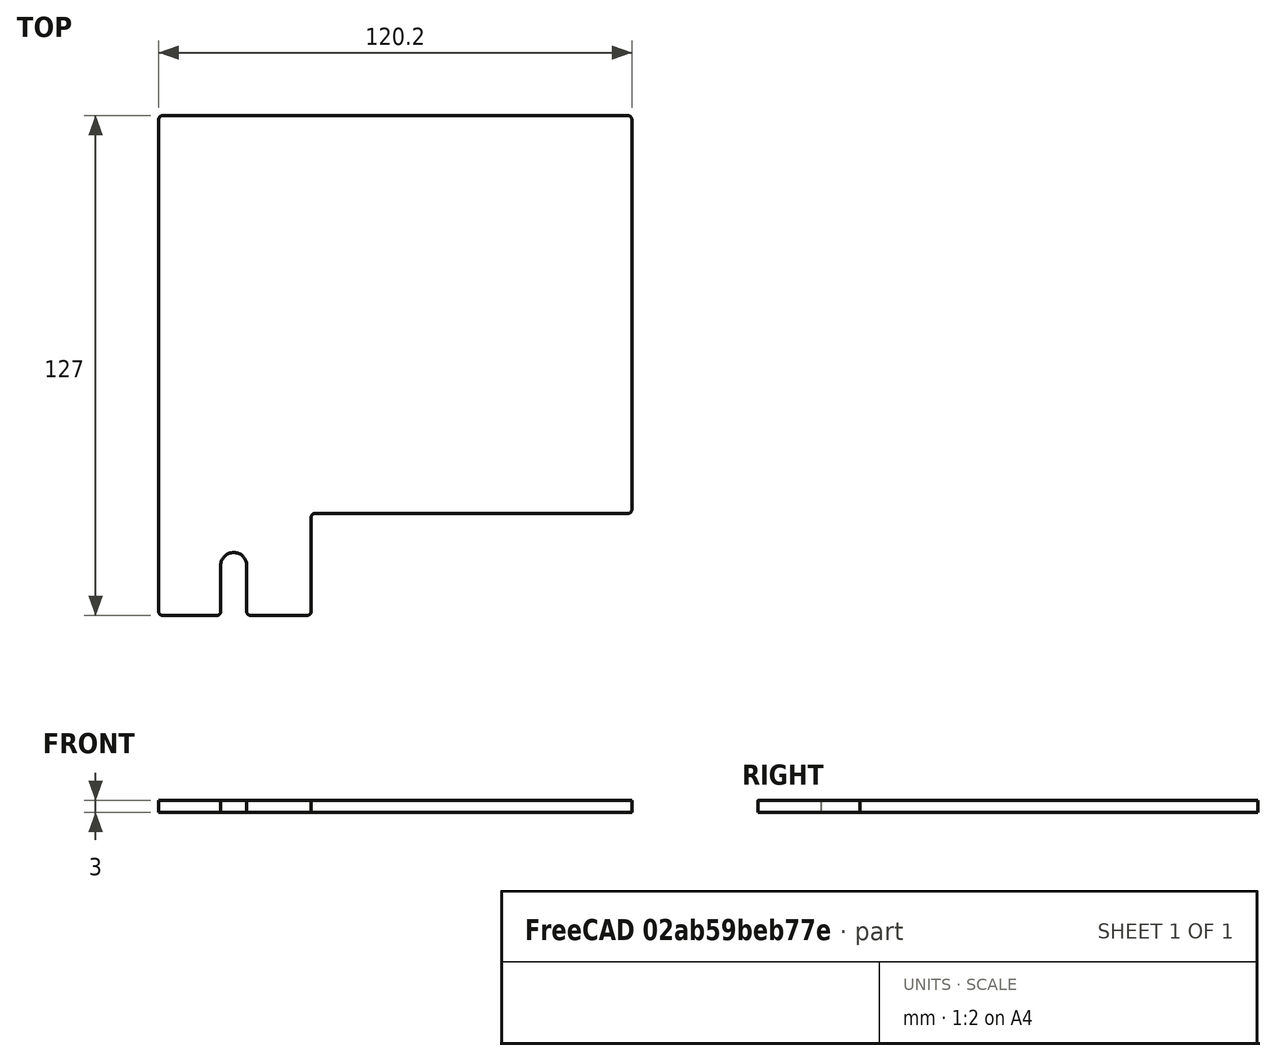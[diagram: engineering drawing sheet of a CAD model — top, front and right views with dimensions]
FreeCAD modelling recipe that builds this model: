
FCSTD DOCUMENT  (FreeCAD 0.21R33675 (Git))
Label: right_wall_front_5in
License: All rights reserved
LicenseURL: http://en.wikipedia.org/wiki/All_rights_reserved
objects: Spreadsheet::Sheet×1, Sketcher::SketchObject×1, PartDesign::Pad×1, PartDesign::Body×1
note: 4 computed .brp shape members not serialized (recipe doc carries the construction recipe); baked Part::Feature solids carry a one-line shape summary decoded from their .brp

FEATURE [Spreadsheet::Sheet] Spreadsheet
  cells = A2='Parameters; A3='Thickness; B3(Thickness)==3 mm; A4='BeamLength; B4(BeamLength)==18 in; A5='BracketLength; B5(BracketLength)==108.6 mm; A6='DistanceLeftBracketEdgeToDoor; B6(DistanceLeftBracketEdgeToDoor)==82.4999 mm; A7='DistanceRightBracketEdgeToDoor; B7(DistanceRightBracketEdgeToDoor)==23.1001 mm; A8='ServoOffsetFromCenter; B8(ServoOffsetFromCenter)==3 in + 1 * (DistanceLeftBracketEdgeToDoor - DistanceRightBracketEdgeToDoor); A9='DoorMargin; B9(DoorMargin)==1 mm; A10='LengthMargin; B10(LengthMargin)==0 mm; A11='LengthLeftBracketEdgeToDoorGap; B11(LengthLeftBracketEdgeToDoorGap)==DistanceLeftBracketEdgeToDoor - DoorMargin; A12='LengthRightBracketEdgeToDoorGap; B12(LengthRightBracketEdgeToDoorGap)==DistanceRightBracketEdgeToDoor - DoorMargin; A13='LengthDoorGap; B13(LengthDoorGap)==BracketLength - LengthLeftBracketEdgeToDoorGap - LengthRightBracketEdgeToDoorGap; A14='BeamLengthMinusBracketLength; B14(BeamLengthMinusBracketLength)==BeamLength - BracketLength; A15='DistanceFrontToDoor; B15(DistanceFrontToDoor)==0.5 * BeamLengthMinusBracketLength + LengthLeftBracketEdgeToDoorGap - ServoOffsetFromCenter; A16='DistanceFrontToBracket; B16(DistanceFrontToBracket)==0.5 * BeamLengthMinusBracketLength - ServoOffsetFromCenter; A17='LengthFrontToDoor; B17(LengthFrontToDoor)==DistanceFrontToDoor - LengthMargin; A18='LengthFrontToBracket; B18(LengthFrontToBracket)==DistanceFrontToBracket - LengthMargin; A19='Height; B19(Height)==5 in; A20='CutoutMargin; B20(CutoutMargin)==0.5 mm; A21='CutoutHeight; B21(CutoutHeight)==1 in + CutoutMargin; A22='FilletRadius; B22(FilletRadius)==1 mm; A23='MountHoleDiameter; B23(MountHoleDiameter)==0.26 in; A24='MountHoleDistanceFromBottom; B24(MountHoleDistanceFromBottom)==0.5 in; A25='MountHoleSideMargin; B25(MountHoleSideMargin)==0.75 in; B27==3 in + DistanceLeftBracketEdgeToDoor + 0.5 * Thickness - 0.5 * BracketLength
FEATURE [Sketcher::SketchObject] Sketch
  FullyConstrained = true
  MapMode = 5
  Support = -> [XY_Plane]
  expr: Constraints[14] = Spreadsheet.FilletRadius
  expr: Constraints[20] = Spreadsheet.Height
  expr: Constraints[48] = Spreadsheet.MountHoleSideMargin
  expr: Constraints[68] = Spreadsheet.MountHoleDiameter
  expr: Constraints[69] = Spreadsheet.MountHoleDistanceFromBottom
  expr: Constraints[7] = Spreadsheet.LengthFrontToDoor
  expr: Constraints[8] = Spreadsheet.LengthFrontToBracket
  expr: Constraints[9] = Spreadsheet.CutoutHeight
  sketch-geometry (30):
    g0: LineSegment StartX=0 StartY=126 StartZ=0 EndX=0 EndY=1 EndZ=0
    g1: LineSegment StartX=1 StartY=0 StartZ=0 EndX=37.7002 EndY=0 EndZ=0
    g2: LineSegment StartX=38.7002 StartY=1 StartZ=0 EndX=38.7002 EndY=24.9 EndZ=0
    g3: LineSegment StartX=39.7002 StartY=25.9 StartZ=0 EndX=119.2 EndY=25.9 EndZ=0
    g4: LineSegment StartX=120.2 StartY=26.9 StartZ=0 EndX=120.2 EndY=126 EndZ=0
    g5: LineSegment StartX=119.2 StartY=127 StartZ=0 EndX=1 EndY=127 EndZ=0
    g6: ArcOfCircle CenterX=1 CenterY=126 CenterZ=0 NormalX=0 NormalY=0 NormalZ=1 AngleXU=0 Radius=1 StartAngle=1.5708 EndAngle=3.14159
    g7: GeomPoint X=0 Y=127 Z=0
    g8: ArcOfCircle CenterX=1 CenterY=1 CenterZ=0 NormalX=0 NormalY=0 NormalZ=1 AngleXU=0 Radius=1 StartAngle=3.14159 EndAngle=4.71239
    g9: GeomPoint X=0 Y=0 Z=0
    g10: ArcOfCircle CenterX=37.7002 CenterY=1 CenterZ=0 NormalX=0 NormalY=0 NormalZ=1 AngleXU=0 Radius=1 StartAngle=4.71239 EndAngle=6.28319
    g11: GeomPoint X=38.7002 Y=0 Z=0
    g12: ArcOfCircle CenterX=39.7002 CenterY=24.9 CenterZ=0 NormalX=0 NormalY=0 NormalZ=1 AngleXU=0 Radius=1 StartAngle=1.5708 EndAngle=3.14159
    g13: GeomPoint X=38.7002 Y=25.9 Z=0
    g14: ArcOfCircle CenterX=119.2 CenterY=26.9 CenterZ=0 NormalX=0 NormalY=0 NormalZ=1 AngleXU=0 Radius=1 StartAngle=4.71239 EndAngle=6.28319
    g15: GeomPoint X=120.2 Y=25.9 Z=0
    g16: ArcOfCircle CenterX=119.2 CenterY=126 CenterZ=0 NormalX=0 NormalY=0 NormalZ=1 AngleXU=0 Radius=1 StartAngle=-3.7375e-12 EndAngle=1.5708
    g17: GeomPoint X=120.2 Y=127 Z=0
    g18: GeomPoint X=19.3501 Y=0 Z=0
    g19: LineSegment StartX=19.05 StartY=0 StartZ=0 EndX=19.05 EndY=12.7 EndZ=0
    g20: Circle CenterX=19.05 CenterY=12.7 CenterZ=0 NormalX=0 NormalY=0 NormalZ=1 AngleXU=0 Radius=3.302
    g21: LineSegment StartX=19.05 StartY=12.7 StartZ=0 EndX=0 EndY=12.7 EndZ=0
    g22: ArcOfCircle CenterX=19.05 CenterY=12.7 CenterZ=0 NormalX=0 NormalY=0 NormalZ=1 AngleXU=0 Radius=3.302 StartAngle=0 EndAngle=3.14159
    g23: LineSegment StartX=19.05 StartY=12.7 StartZ=0 EndX=22.352 EndY=12.7 EndZ=0
    g24: LineSegment StartX=15.748 StartY=12.7 StartZ=0 EndX=15.748 EndY=1 EndZ=0
    g25: LineSegment StartX=22.352 StartY=12.7 StartZ=0 EndX=22.352 EndY=1 EndZ=0
    g26: ArcOfCircle CenterX=14.748 CenterY=1 CenterZ=0 NormalX=0 NormalY=0 NormalZ=1 AngleXU=0 Radius=1 StartAngle=4.71239 EndAngle=6.28319
    g27: ArcOfCircle CenterX=23.352 CenterY=1 CenterZ=0 NormalX=0 NormalY=0 NormalZ=1 AngleXU=0 Radius=1 StartAngle=3.14159 EndAngle=4.71239
    g28: LineSegment StartX=1 StartY=0 StartZ=0 EndX=14.748 EndY=0 EndZ=0
    g29: LineSegment StartX=23.352 StartY=0 StartZ=0 EndX=37.7002 EndY=0 EndZ=0
  constraints (71):
    c: Vertical(g0)
    c: Horizontal(g1)
    c: Vertical(g2)
    c: Horizontal(g3)
    c: Vertical(g4)
    c: Horizontal(g5)
    c: Coincident(g-1,g9)
    c: DistanceX(g7,g17) = 120.2
    c: DistanceX(g9,g11) = 38.7002
    c: DistanceY(g11,g13) = 25.9
    c: PointOnObject(g7,g0)
    c: PointOnObject(g7,g5)
    c: Tangent(g0,g6) = -1.5708
    c: Tangent(g5,g6) = -1.5708
    c: Radius(g6) = 1
    c: PointOnObject(g9,g0)
    c: PointOnObject(g9,g1)
    c: Tangent(g0,g8) = -1.5708
    c: Tangent(g1,g8) = -1.5708
    c: Equal(g8,g6)
    c: DistanceY(g1,g5) = 127
    c: PointOnObject(g11,g1)
    c: PointOnObject(g11,g2)
    c: Tangent(g1,g10) = -1.5708
    c: Tangent(g2,g10) = -1.5708
    c: Equal(g10,g8)
    c: PointOnObject(g13,g2)
    c: PointOnObject(g13,g3)
    c: Tangent(g2,g12) = 1.5708
    c: Tangent(g3,g12) = 1.5708
    c: Equal(g12,g10)
    c: PointOnObject(g15,g3)
    c: PointOnObject(g15,g4)
    c: Tangent(g3,g14) = -1.5708
    c: Tangent(g4,g14) = -1.5708
    c: Equal(g14,g12)
    c: PointOnObject(g17,g5)
    c: PointOnObject(g17,g4)
    c: Tangent(g5,g16) = -1.5708
    c: Tangent(g4,g16) = -1.5708
    c: Equal(g16,g14)
    c: Symmetric(g1,g1,g18)
    c: Vertical(g19)
    c: PointOnObject(g19,g1)
    c: Coincident(g20,g19)
    c: Coincident(g21,g20)
    c: PointOnObject(g21,g0)
    c: Horizontal(g21)
    c: DistanceX(g21,g21) = 19.05
    c: Coincident(g22,g19)
    c: PointOnObject(g22,g21)
    c: Coincident(g23,g22)
    c: Coincident(g23,g22)
    c: Horizontal(g23)
    c: PointOnObject(g22,g20)
    c: Coincident(g24,g22)
    c: Vertical(g24)
    c: Coincident(g25,g22)
    c: Vertical(g25)
    c: Equal(g24,g25)
    c: Tangent(g26,g24) = 1.5708
    c: Tangent(g26,g1) = -1.5708
    c: Tangent(g27,g25) = -1.5708
    c: Tangent(g27,g1) = -1.5708
    c: Equal(g26,g8)
    c: Coincident(g28,g8)
    c: Coincident(g28,g26)
    c: Coincident(g29,g27)
    c: Diameter(g22) = 6.604
    c: DistanceY(g26,g22) = 12.7
    c: Coincident(g29,g10)
FEATURE [PartDesign::Pad] Pad
  Direction = (0,0,1)
  Length = 3
  Length2 = 10
  Profile = -> Sketch
  ReferenceAxis = -> Sketch [N_Axis]
  Type = 0
  expr: Length = Spreadsheet.Thickness
FEATURE [PartDesign::Body] Body
  Group = -> [Sketch,Pad]
  Origin = -> Origin
  Tip = -> Pad
